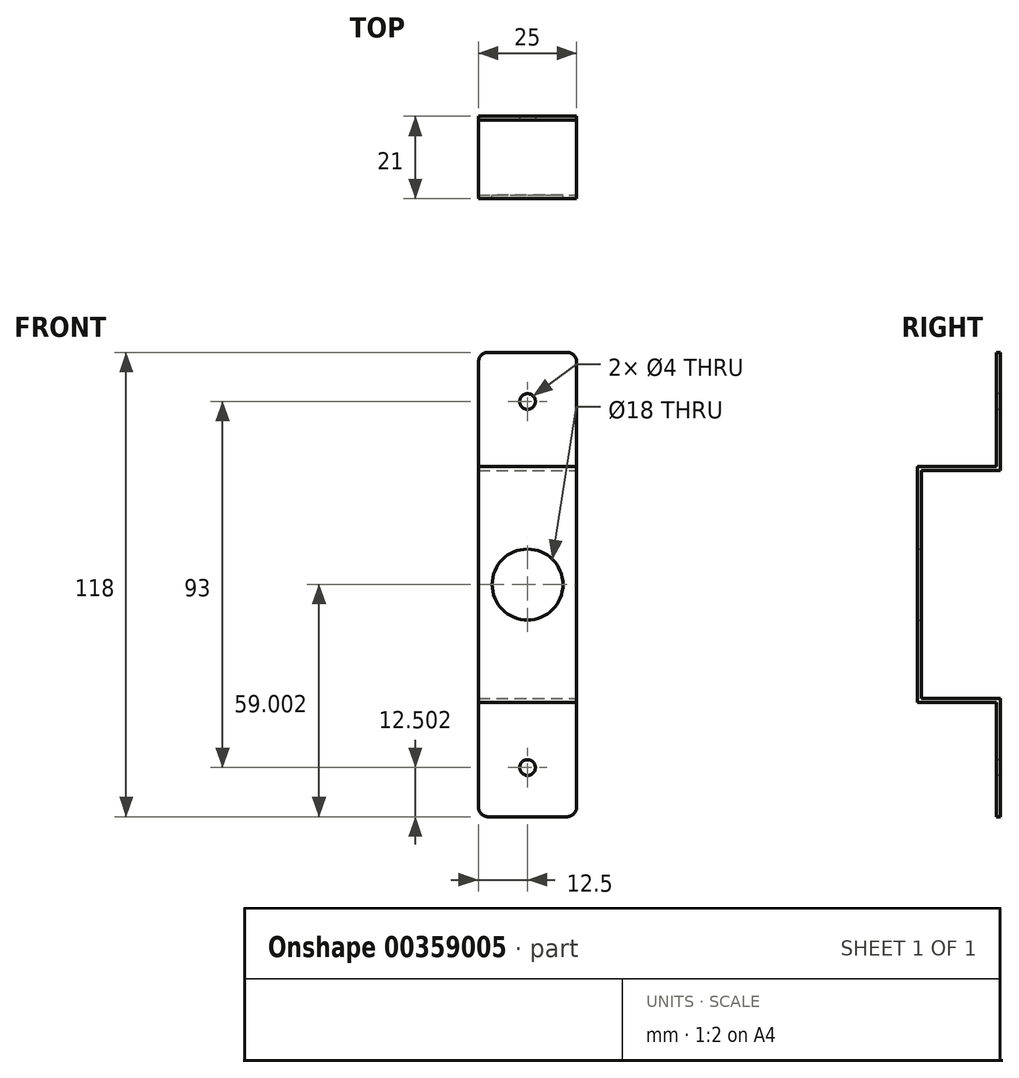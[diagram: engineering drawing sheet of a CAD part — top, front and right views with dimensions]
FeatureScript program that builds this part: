
annotation { "Feature Type Name" : "Feature", "Feature Type Description" : "" }
export const myFeature = defineFeature(function(context is Context, id is Id, definition is map)
    precondition{}
    {
        {
            var Q0;
            Q0=qCreatedBy(makeId("Right.planeOp"),FACE);
            var sketch = newSketch(context, id + "F0", { "sketchPlane" : qUnion([Q0])});
            skLineSegment(sketch, "E0", {"start": v(0, 86.23) * mm, "end": v(0, 57.23) * mm});
            skLineSegment(sketch, "E1", {"start": v(0, 57.23) * mm, "end": v(0, 57.23) * mm});
            skLineSegment(sketch, "E2", {"start": v(0, 57.23) * mm, "end": v(-20, 57.23) * mm});
            skLineSegment(sketch, "E3", {"start": v(-20, 57.23) * mm, "end": v(-20, 57.23) * mm});
            skLineSegment(sketch, "E4", {"start": v(-20, -2.77) * mm, "end": v(-20, 57.23) * mm});
            skLineSegment(sketch, "E5", {"start": v(-20, -2.77) * mm, "end": v(0, -2.77) * mm});
            skLineSegment(sketch, "E6", {"start": v(0, -2.77) * mm, "end": v(0, -2.77) * mm});
            skLineSegment(sketch, "E7", {"start": v(0, -2.77) * mm, "end": v(0, -31.77) * mm});
            skLineSegment(sketch, "E8", {"start": v(0, -31.77) * mm, "end": v(0, -31.77) * mm});
            skLineSegment(sketch, "E9", {"start": v(0, -31.77) * mm, "end": v(1, -31.77) * mm});
            skLineSegment(sketch, "E10", {"start": v(1, -31.77) * mm, "end": v(1, -31.77) * mm});
            skLineSegment(sketch, "E11", {"start": v(1, -31.77) * mm, "end": v(1, -1.77) * mm});
            skLineSegment(sketch, "E12", {"start": v(1, -1.77) * mm, "end": v(1, -1.77) * mm});
            skLineSegment(sketch, "E13", {"start": v(1, -1.77) * mm, "end": v(-19, -1.77) * mm});
            skLineSegment(sketch, "E14", {"start": v(-19, -1.77) * mm, "end": v(-19, -1.77) * mm});
            skLineSegment(sketch, "E15", {"start": v(-19, -1.77) * mm, "end": v(-19, 56.23) * mm});
            skLineSegment(sketch, "E16", {"start": v(-19, 56.23) * mm, "end": v(-19, 56.23) * mm});
            skLineSegment(sketch, "E17", {"start": v(-19, 56.23) * mm, "end": v(1, 56.23) * mm});
            skLineSegment(sketch, "E18", {"start": v(1, 56.23) * mm, "end": v(1, 56.23) * mm});
            skLineSegment(sketch, "E19", {"start": v(1, 56.23) * mm, "end": v(1, 86.23) * mm});
            skLineSegment(sketch, "E20", {"start": v(1, 86.23) * mm, "end": v(1, 86.23) * mm});
            skLineSegment(sketch, "E21", {"start": v(1, 86.23) * mm, "end": v(0, 86.23) * mm});
            skSolve(sketch);
        }
        {
            var Q0;
            Q0=makeQuery(id+"F0.imprint","IMPRINT",FACE,{"disambiguationData":[TD([[makeQuery(id+"F0.imprint","IMPRINT",EDGE,{"derivedFrom":sQuery(id+"F0.wireOp",EDGE,"E0")}),1.0]])]});
            extrude(context, id + "F1", {"entities" : qUnion([Q0]), "oppositeDirection" : true, "depth" : 25 * mm});
        }
        {
            var Q0;
            Q0=makeQuery(id+"F1.opExtrude","CAP_EDGE",EDGE,{"disambiguationData":[OSD([sQuery(id+"F0.wireOp",EDGE,"E21")])],"isStart":true});
            var Q1;
            Q1=makeQuery(id+"F1.opExtrude","CAP_EDGE",EDGE,{"disambiguationData":[OSD([sQuery(id+"F0.wireOp",EDGE,"E21")])],"isStart":false});
            var Q2;
            Q2=makeQuery(id+"F1.opExtrude","CAP_EDGE",EDGE,{"disambiguationData":[OSD([sQuery(id+"F0.wireOp",EDGE,"E9")])],"isStart":true});
            var Q3;
            Q3=makeQuery(id+"F1.opExtrude","CAP_EDGE",EDGE,{"disambiguationData":[OSD([sQuery(id+"F0.wireOp",EDGE,"E9")])],"isStart":false});
            fillet(context, id + "F2", {"entities" : qUnion([Q0, Q1, Q2, Q3]), "radius" : 2.54 * mm, "tangentPropagation" : true, "allowEdgeOverflow" : false});
        }
        {
            var Q0;
            Q0=qCreatedBy(makeId("Front.planeOp"),FACE);
            var sketch = newSketch(context, id + "F3", { "sketchPlane" : qUnion([Q0])});
            skPoint(sketch, "E22", {"position": v(-12.5, 27.23) * mm});
            skSolve(sketch);
        }
        {
            var Q0;
            Q0=sQuery(id+"F3.wireOp",VERTEX,"E22");
            var Q1;
            Q1=makeQuery(id+"F1.opExtrude","SWEPT_BODY",BODY,{"disambiguationData":[OSD([sQuery(id+"F0.wireOp",EDGE,"E0"),sQuery(id+"F0.wireOp",EDGE,"E2"),sQuery(id+"F0.wireOp",EDGE,"E4"),sQuery(id+"F0.wireOp",EDGE,"E5"),sQuery(id+"F0.wireOp",EDGE,"E7"),sQuery(id+"F0.wireOp",EDGE,"E9"),sQuery(id+"F0.wireOp",EDGE,"E11"),sQuery(id+"F0.wireOp",EDGE,"E13"),sQuery(id+"F0.wireOp",EDGE,"E15"),sQuery(id+"F0.wireOp",EDGE,"E17"),sQuery(id+"F0.wireOp",EDGE,"E19"),sQuery(id+"F0.wireOp",EDGE,"E21")])]});
            hole(context, id + "F4", {"style" : HoleStyle.SIMPLE, "endStyle" : HoleEndStyle.THROUGH, "oppositeDirection" : true, "holeDiameter" : 18 * mm, "isTappedThrough" : true, "tappedDepth" : 12 * mm, "tapClearance" : 3, "locations" : qUnion([Q0]), "scope" : qUnion([Q1])});
        }
        {
            var Q0;
            Q0=qCreatedBy(makeId("Front.planeOp"),FACE);
            var sketch = newSketch(context, id + "F5", { "sketchPlane" : qUnion([Q0])});
            skPoint(sketch, "E23", {"position": v(-12.5, 73.73) * mm});
            skPoint(sketch, "E24", {"position": v(-12.5, -19.27) * mm});
            skSolve(sketch);
        }
        {
            var Q0;
            Q0=sQuery(id+"F5.wireOp",VERTEX,"E23");
            var Q1;
            Q1=sQuery(id+"F5.wireOp",VERTEX,"E24");
            var Q2;
            Q2=makeQuery(id+"F1.opExtrude","SWEPT_BODY",BODY,{"disambiguationData":[OSD([sQuery(id+"F0.wireOp",EDGE,"E0"),sQuery(id+"F0.wireOp",EDGE,"E2"),sQuery(id+"F0.wireOp",EDGE,"E4"),sQuery(id+"F0.wireOp",EDGE,"E5"),sQuery(id+"F0.wireOp",EDGE,"E7"),sQuery(id+"F0.wireOp",EDGE,"E9"),sQuery(id+"F0.wireOp",EDGE,"E11"),sQuery(id+"F0.wireOp",EDGE,"E13"),sQuery(id+"F0.wireOp",EDGE,"E15"),sQuery(id+"F0.wireOp",EDGE,"E17"),sQuery(id+"F0.wireOp",EDGE,"E19"),sQuery(id+"F0.wireOp",EDGE,"E21")])]});
            hole(context, id + "F6", {"style" : HoleStyle.SIMPLE, "endStyle" : HoleEndStyle.THROUGH, "holeDiameter" : 4 * mm, "isTappedThrough" : true, "tappedDepth" : 12 * mm, "tapClearance" : 3, "locations" : qUnion([Q0, Q1]), "scope" : qUnion([Q2])});
        }
    });
